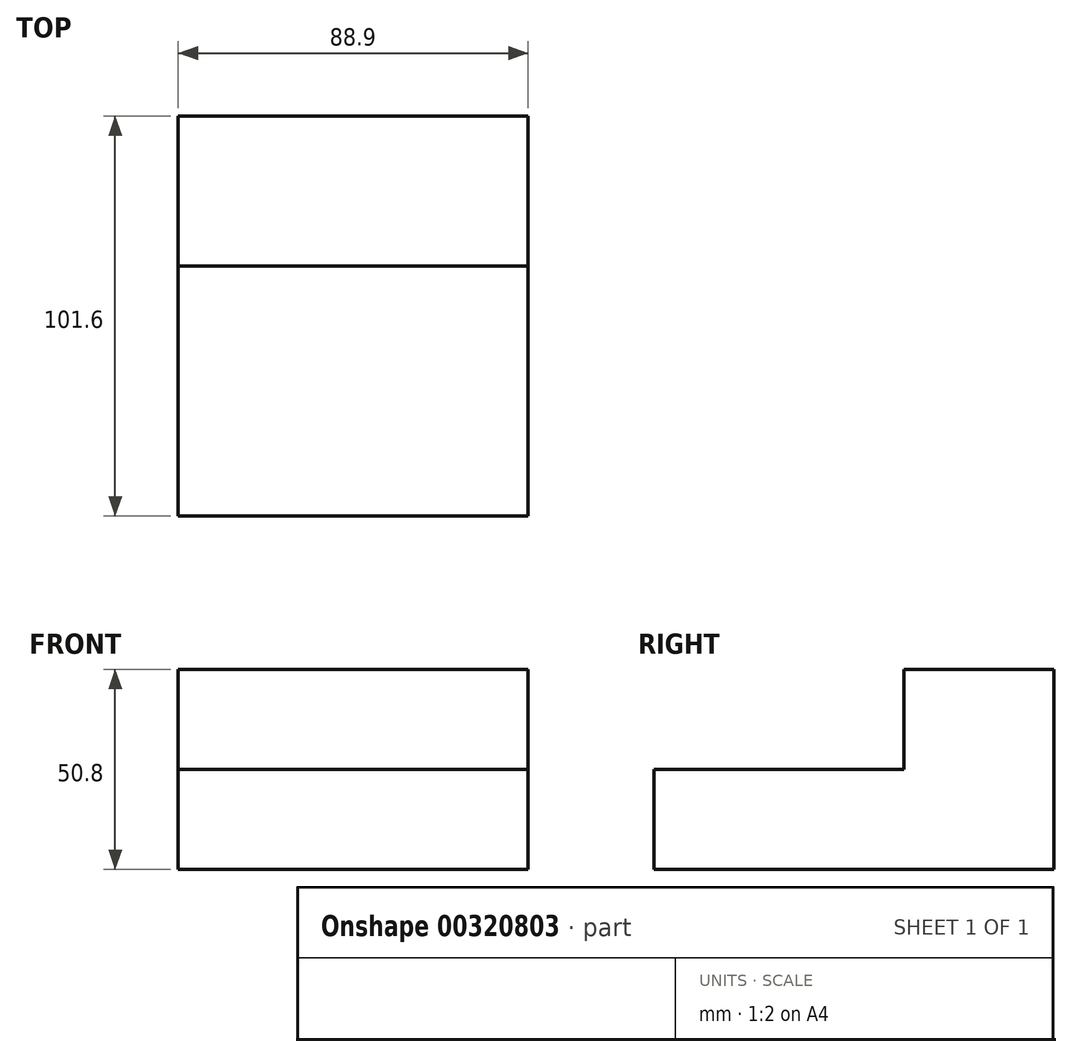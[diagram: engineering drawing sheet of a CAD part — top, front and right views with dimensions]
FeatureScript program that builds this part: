
annotation { "Feature Type Name" : "Feature", "Feature Type Description" : "" }
export const myFeature = defineFeature(function(context is Context, id is Id, definition is map)
    precondition{}
    {
        {
            var Q0;
            Q0=qCreatedBy(makeId("Right.planeOp"),FACE);
            var sketch = newSketch(context, id + "F0", { "sketchPlane" : qUnion([Q0])});
            skLineSegment(sketch, "E0", {"start": v(-41.62, -34.47) * mm, "end": v(59.98, -34.47) * mm});
            skLineSegment(sketch, "E1", {"start": v(59.98, -34.47) * mm, "end": v(59.98, 16.33) * mm});
            skLineSegment(sketch, "E2", {"start": v(59.98, 16.33) * mm, "end": v(21.88, 16.33) * mm});
            skLineSegment(sketch, "E3", {"start": v(21.88, 16.33) * mm, "end": v(21.88, -9.07) * mm});
            skLineSegment(sketch, "E4", {"start": v(21.88, -9.07) * mm, "end": v(-41.62, -9.07) * mm});
            skLineSegment(sketch, "E5", {"start": v(-41.62, -9.07) * mm, "end": v(-41.62, -34.47) * mm});
            skSolve(sketch);
        }
        {
            var Q0;
            Q0=makeQuery(id+"F0.imprint","IMPRINT",FACE,{"disambiguationData":[TD([[makeQuery(id+"F0.imprint","IMPRINT",EDGE,{"derivedFrom":sQuery(id+"F0.wireOp",EDGE,"E0")}),1.0]])]});
            extrude(context, id + "F1", {"entities" : qUnion([Q0]), "depth" : 88.9 * mm});
        }
    });
